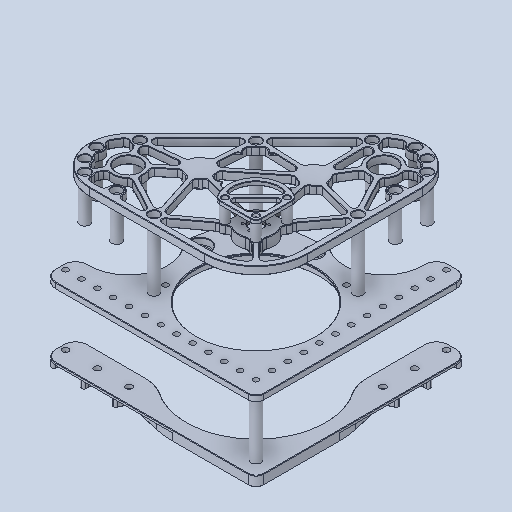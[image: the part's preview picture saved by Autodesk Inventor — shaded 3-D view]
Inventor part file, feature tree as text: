
AUTODESK INVENTOR PART (.ipt)
format: ipt  version: 2023.4 (Build 274418000, 418)  size: 1,542,656 bytes
history: native  units: in
note: dims shown in document units (in); Inventor stores cm internally (conversion verified against a paired STEP export)
features: other x15, chamfer x4
ambient origin geometry x8: Origin, YZ Plane, XZ Plane, XY Plane, X Axis, Y Axis, Z Axis, Center Point
bodies: Solid1 (feature_tree), Solid2 (feature_tree), Solid3 (feature_tree), Solid4 (feature_tree), Solid5 (feature_tree), Solid6 (feature_tree), Solid7 (feature_tree), Solid8 (feature_tree), Solid9 (feature_tree), Solid10 (feature_tree), Solid11 (feature_tree), Solid12 (feature_tree), Solid13 (feature_tree), Solid14 (feature_tree), Solid15 (feature_tree), Solid16 (feature_tree), Solid17 (feature_tree), Solid18 (feature_tree), Solid19 (feature_tree)
feature tree (19):
  other  "Boss-Extrude4[1]"
  other  "Boss-Extrude4[2]"
  other  "Boss-Extrude4[3]"
  other  "Boss-Extrude6[1]"
  other  "Boss-Extrude6[2]"
  other  "Boss-Extrude6[3]"
  other  "Boss-Extrude6[4]"
  other  "Boss-Extrude6[5]"
  other  "Boss-Extrude6[6]"
  other  "Boss-Extrude6[7]"
  other  "Boss-Extrude6[8]"
  other  "Boss-Extrude9[1]"
  other  "Boss-Extrude17[1]"
  other  "Boss-Extrude17[2]"
  other  "Boss-Extrude17[3]"
  chamfer  "Chamfer4"  [1 undecoded]
  chamfer  "Chamfer1"  [1 undecoded]
  chamfer  "Chamfer3"  [1 undecoded]
  chamfer  "Chamfer2"  [1 undecoded]
note: 4 required parameter values undecoded (feature->parameter linkage not recoverable at this tier; creation-order binding heuristic only, values carry confidence <= 0.55)
